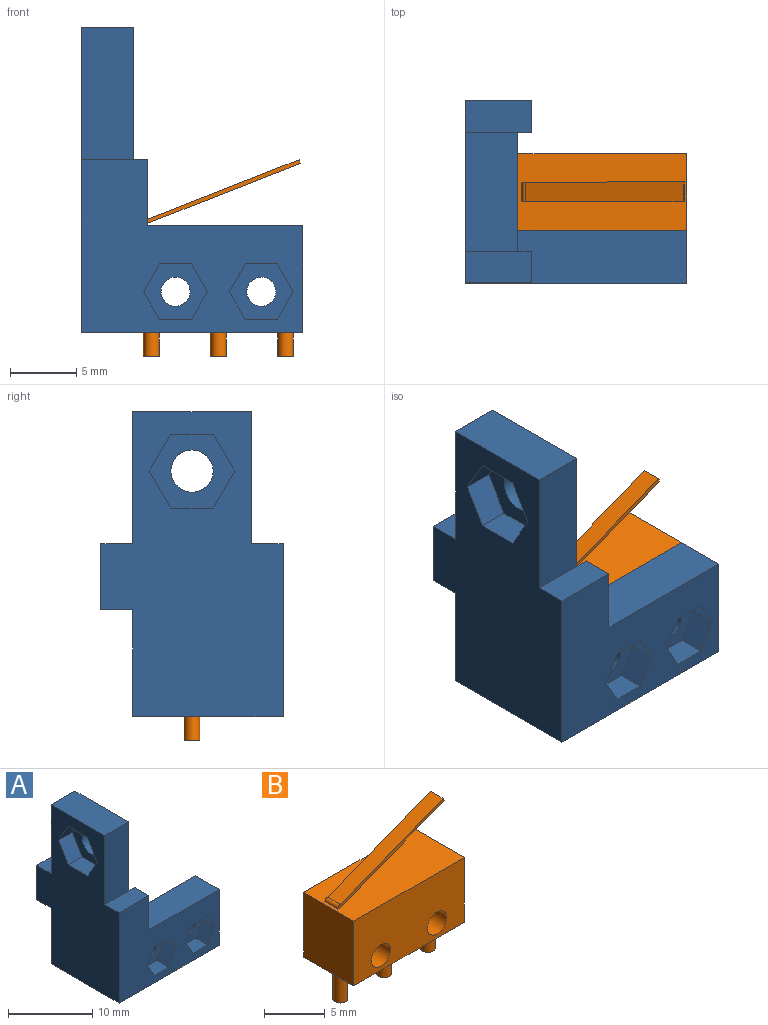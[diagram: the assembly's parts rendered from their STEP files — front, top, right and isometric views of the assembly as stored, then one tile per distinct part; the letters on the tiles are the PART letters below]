
ASSEMBLY  parts=2 mates=1
PART A: 43 faces, bbox 16.8x13.8x23.1 mm
  f0: plane 10x4mm, normal (0,1,0), area 40mm2, adj f3,f25,f27,f39
  f1: plane 10x4mm, normal (0,-1,0), area 40mm2, adj f3,f25,f27,f36
  f2: cylinder r=1.6mm len=3.2mm, axis (1,0,0), area 17.1mm2, adj f27,f34
  f3: plane 23.1x13.8mm, normal (-1,0,0), area 224.2mm2, adj f0,f1,f6,f7,f25,f26,f28,f29
  f4: cylinder r=1.1mm len=2.2mm, axis (0,1,0), area 13.8mm2, adj f10,f17
  f5: cylinder r=1.1mm len=2.2mm, axis (0,1,0), area 13.8mm2, adj f10,f24
  f6: plane 16.8x13.1mm, normal (0,-1,0), area 130.5mm2, adj f3,f7,f8,f9,f11,f12,f13,f14
  f7: plane 16.8x11.4mm, normal (0,0,-1), area 96.8mm2, adj f3,f6,f8,f10,f26,f27
  f8: plane 8.1x4mm, normal (1,0,0), area 32.4mm2, adj f6,f7,f9,f10
  f9: plane 12.8x4mm, normal (0,0,1), area 48.8mm2, adj f6,f8,f10,f27,f35,f37
  f10: plane 12.8x8.1mm, normal (0,1,0), area 96.1mm2, adj f4,f5,f7,f8,f9,f27
  f11: plane 2.1x2mm, normal (-0.87,0,0.5), area 4.8mm2, adj f6,f12,f16,f17
  f12: plane 2.1x2mm, normal (-0.87,0,-0.5), area 4.8mm2, adj f6,f11,f13,f17
  f13: plane 2.43x2mm, normal (0,0,-1), area 4.8mm2, adj f6,f12,f14,f17
  f14: plane 2.1x2mm, normal (0.87,0,-0.5), area 4.8mm2, adj f6,f13,f15,f17
  f15: plane 2.1x2mm, normal (0.87,0,0.5), area 4.8mm2, adj f6,f14,f16,f17
  f16: plane 2.43x2mm, normal (0,0,1), area 4.8mm2, adj f6,f11,f15,f17
  f17: plane 4.85x4.2mm, normal (0,-1,0), area 11.5mm2, adj f4,f11,f12,f13,f14,f15,f16
  f18: plane 2.1x2mm, normal (-0.87,0,0.5), area 4.8mm2, adj f6,f19,f23,f24
  f19: plane 2.1x2mm, normal (-0.87,0,-0.5), area 4.8mm2, adj f6,f18,f20,f24
  f20: plane 2.43x2mm, normal (0,0,-1), area 4.8mm2, adj f6,f19,f21,f24
  f21: plane 2.1x2mm, normal (0.87,0,-0.5), area 4.8mm2, adj f6,f20,f22,f24
  f22: plane 2.1x2mm, normal (0.87,0,0.5), area 4.8mm2, adj f6,f21,f23,f24
  f23: plane 2.43x2mm, normal (0,0,1), area 4.8mm2, adj f6,f18,f22,f24
  f24: plane 4.85x4.2mm, normal (0,-1,0), area 11.5mm2, adj f5,f18,f19,f20,f21,f22,f23
  f25: plane 9x4mm, normal (0,0,1), area 36mm2, adj f0,f1,f3,f27
  f26: plane 8.1x4mm, normal (0,1,0), area 32.4mm2, adj f3,f7,f27,f41
  f27: plane 23.1x9mm, normal (1,0,0), area 186.9mm2, adj f0,f1,f2,f7,f9,f10,f25,f26
  f28: plane 2.8x2.3mm, normal (0,0.87,0.5), area 7.4mm2, adj f3,f29,f33,f34
  f29: plane 2.8x2.3mm, normal (0,0.87,-0.5), area 7.4mm2, adj f3,f28,f30,f34
  f30: plane 3.23x2.3mm, normal (0,0,-1), area 7.4mm2, adj f3,f29,f31,f34
  f31: plane 2.8x2.3mm, normal (0,-0.87,-0.5), area 7.4mm2, adj f3,f30,f32,f34
  f32: plane 2.8x2.3mm, normal (0,-0.87,0.5), area 7.4mm2, adj f3,f31,f33,f34
  f33: plane 3.23x2.3mm, normal (0,0,1), area 7.4mm2, adj f3,f28,f32,f34
  f34: plane 6.47x5.6mm, normal (-1,0,0), area 19.1mm2, adj f2,f28,f29,f30,f31,f32,f33
  f35: plane 5x1mm, normal (0,1,0), area 5mm2, adj f9,f27,f36,f37
  f36: plane 5x2.4mm, normal (0,0,1), area 12mm2, adj f1,f3,f6,f35,f37
  f37: plane 5x2.4mm, normal (1,0,0), area 12mm2, adj f6,f9,f35,f36
  f38: plane 5x1mm, normal (0,-1,0), area 5mm2, adj f27,f39,f41,f42
  f39: plane 5x2.4mm, normal (0,0,1), area 12mm2, adj f0,f3,f38,f40,f42
  f40: plane 5x5mm, normal (0,1,0), area 25mm2, adj f3,f39,f41,f42
  f41: plane 5x2.4mm, normal (0,0,-1), area 12mm2, adj f3,f26,f38,f40,f42
  f42: plane 5x2.4mm, normal (1,0,0), area 12mm2, adj f38,f39,f40,f41
PART B: 20 faces, bbox 12.8x5.8x14.9 mm
  f0: plane 12.8x5.8mm, normal (0,0,1), area 73.8mm2, adj f1,f3,f6,f7,f14,f17,f18,f19
  f1: plane 6.5x5.8mm, normal (-1,0,0), area 37.7mm2, adj f0,f2,f6,f7
  f2: plane 12.8x5.8mm, normal (0,0,-1), area 70.8mm2, adj f1,f3,f6,f7,f8,f10,f12
  f3: plane 6.5x5.8mm, normal (1,0,0), area 37.7mm2, adj f0,f2,f6,f7
  f4: cylinder r=1.1mm len=5.8mm, axis (0,1,0), area 40.1mm2, adj f6,f7
  f5: cylinder r=1.1mm len=5.8mm, axis (0,1,0), area 40.1mm2, adj f6,f7
  f6: plane 12.8x6.5mm, normal (0,-1,0), area 75.6mm2, adj f0,f1,f2,f3,f4,f5
  f7: plane 12.8x6.5mm, normal (0,1,0), area 75.6mm2, adj f0,f1,f2,f3,f4,f5
  f8: cylinder r=0.6mm len=3.4mm, axis (0,0,1), area 12.8mm2, adj f2,f9
  f9: plane 1.2x1.2mm, normal (0,0,-1), area 1.1mm2, adj f8
  f10: cylinder r=0.6mm len=3.4mm, axis (0,0,1), area 12.8mm2, adj f2,f11
  f11: plane 1.2x1.2mm, normal (0,0,-1), area 1.1mm2, adj f10
  f12: cylinder r=0.6mm len=3.4mm, axis (0,0,1), area 12.8mm2, adj f2,f13
  f13: plane 1.2x1.2mm, normal (0,0,-1), area 1.1mm2, adj f12
  f14: cylinder r=0.3mm len=1.5mm, axis (0,-1,0), area 0.7mm2, adj f0,f15,f18,f19
  f15: plane 11.91x4.7mm, normal (-0.37,0,0.93), area 19.2mm2, adj f14,f16,f18,f19
  f16: plane 1.5x0.28mm, normal (0.93,0,0.37), area 0.4mm2, adj f15,f17,f18,f19
  f17: plane 12.02x4.72mm, normal (0.37,0,-0.93), area 19.4mm2, adj f0,f16,f18,f19
  f18: plane 12.32x5mm, normal (0,1,0), area 3.8mm2, adj f0,f14,f15,f16,f17
  f19: plane 12.32x5mm, normal (0,-1,0), area 3.8mm2, adj f0,f14,f15,f16,f17
PLACE A t=(-11.69,0.73,-2.24)mm fixed
PLACE B t=(-11.69,0.73,-2.24)mm
MATE fastened A.f5 <-> B.f4  axis (0,1,0) through (-8.44,-5.07,-0.74)mm
